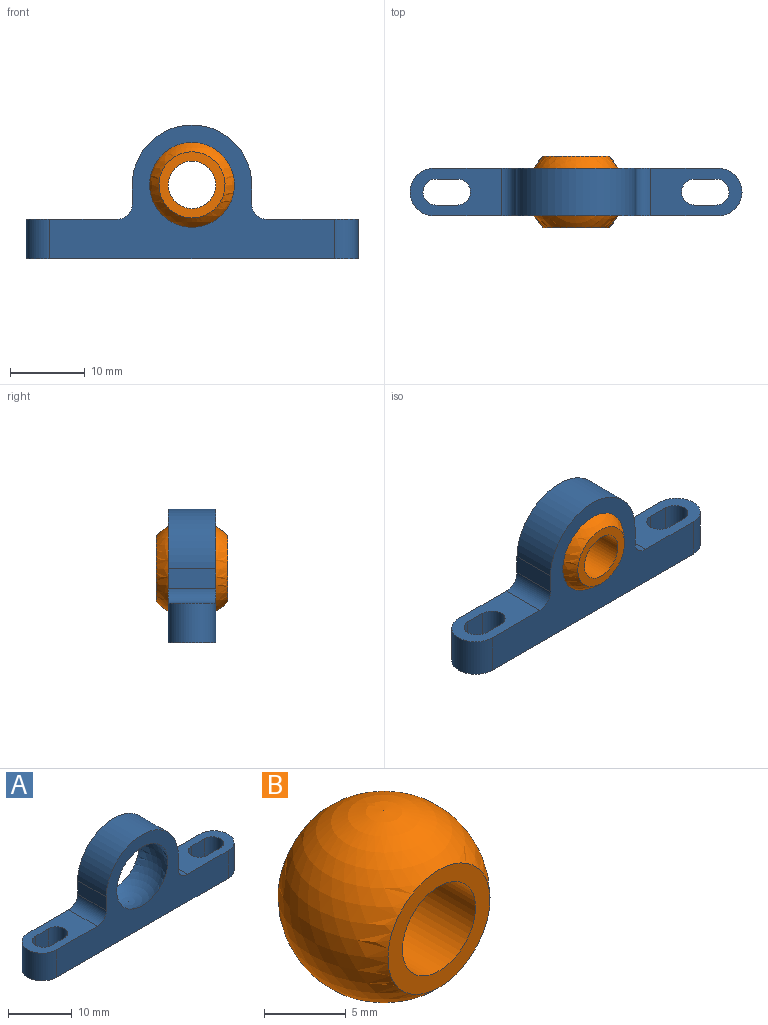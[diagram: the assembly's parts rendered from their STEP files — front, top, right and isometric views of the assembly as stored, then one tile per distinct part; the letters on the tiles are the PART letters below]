
ASSEMBLY  parts=2 mates=1
PART A: 21 faces, bbox 44.5x13x17.9 mm
  f0: cylinder r=8mm len=16mm, axis (0,1,0), area 159.6mm2, adj f7,f17,f18,f20
  f1: sphere r=6.5mm, area 259.3mm2, adj f7,f20
  f2: cylinder r=1.74mm len=5.3mm, axis (0,0,-1), area 29mm2, adj f10,f13,f14,f15
  f3: cylinder r=1.74mm len=5.3mm, axis (0,0,-1), area 29mm2, adj f10,f13,f14,f15
  f4: cylinder r=1.74mm len=5.3mm, axis (0,0,-1), area 29mm2, adj f8,f10,f11,f12
  f5: cylinder r=1.74mm len=5.3mm, axis (0,0,-1), area 29mm2, adj f8,f10,f11,f12
  f6: cylinder r=3.17mm len=6.35mm, axis (0,0,1), area 52.9mm2, adj f7,f8,f10,f20
  f7: plane 38.1x17.91mm, normal (0,-1,0), area 276.9mm2, adj f0,f1,f6,f8,f9,f10,f15,f16
  f8: plane 12.23x6.35mm, normal (0,0,1), area 53.8mm2, adj f4,f5,f6,f7,f11,f12,f19,f20
  f9: cylinder r=3.17mm len=6.35mm, axis (0,0,1), area 52.9mm2, adj f7,f10,f15,f20
  f10: plane 44.45x6.35mm, normal (0,0,-1), area 234.6mm2, adj f2,f3,f4,f5,f6,f7,f9,f11
  f11: plane 5.3x2.87mm, normal (0,1,0), area 15.2mm2, adj f4,f5,f8,f10
  f12: plane 5.3x2.87mm, normal (0,-1,0), area 15.2mm2, adj f4,f5,f8,f10
  f13: plane 5.3x2.87mm, normal (0,1,0), area 15.2mm2, adj f2,f3,f10,f15
  f14: plane 5.3x2.87mm, normal (0,-1,0), area 15.2mm2, adj f2,f3,f10,f15
  f15: plane 12.23x6.35mm, normal (0,0,1), area 53.8mm2, adj f2,f3,f7,f9,f13,f14,f16,f20
  f16: cylinder r=2mm len=6.35mm, axis (0,1,0), area 19.9mm2, adj f7,f15,f17,f20
  f17: plane 6.35x2.61mm, normal (-1,0,0), area 16.6mm2, adj f0,f7,f16,f20
  f18: plane 6.35x2.61mm, normal (1,0,0), area 16.6mm2, adj f0,f7,f19,f20
  f19: cylinder r=2mm len=6.35mm, axis (0,1,0), area 19.9mm2, adj f7,f8,f18,f20
  f20: plane 38.1x17.91mm, normal (0,1,0), area 276.9mm2, adj f0,f1,f6,f8,f9,f10,f15,f16
PART B: 4 faces, bbox 13x13x13 mm
  f0: sphere r=6.5mm, area 389.2mm2, adj f2,f3
  f1: cylinder r=3.17mm len=9.53mm, axis (0,-1,0), area 190.1mm2, adj f2,f3
  f2: plane 8.84x8.84mm, normal (0,-1,0), area 29.7mm2, adj f0,f1
  f3: plane 8.84x8.84mm, normal (0,1,0), area 29.7mm2, adj f0,f1
PLACE A at identity fixed
PLACE B at identity
MATE ball A.f0 <-> B.f1  axis (0,-1,0) through (0,0,0)mm
